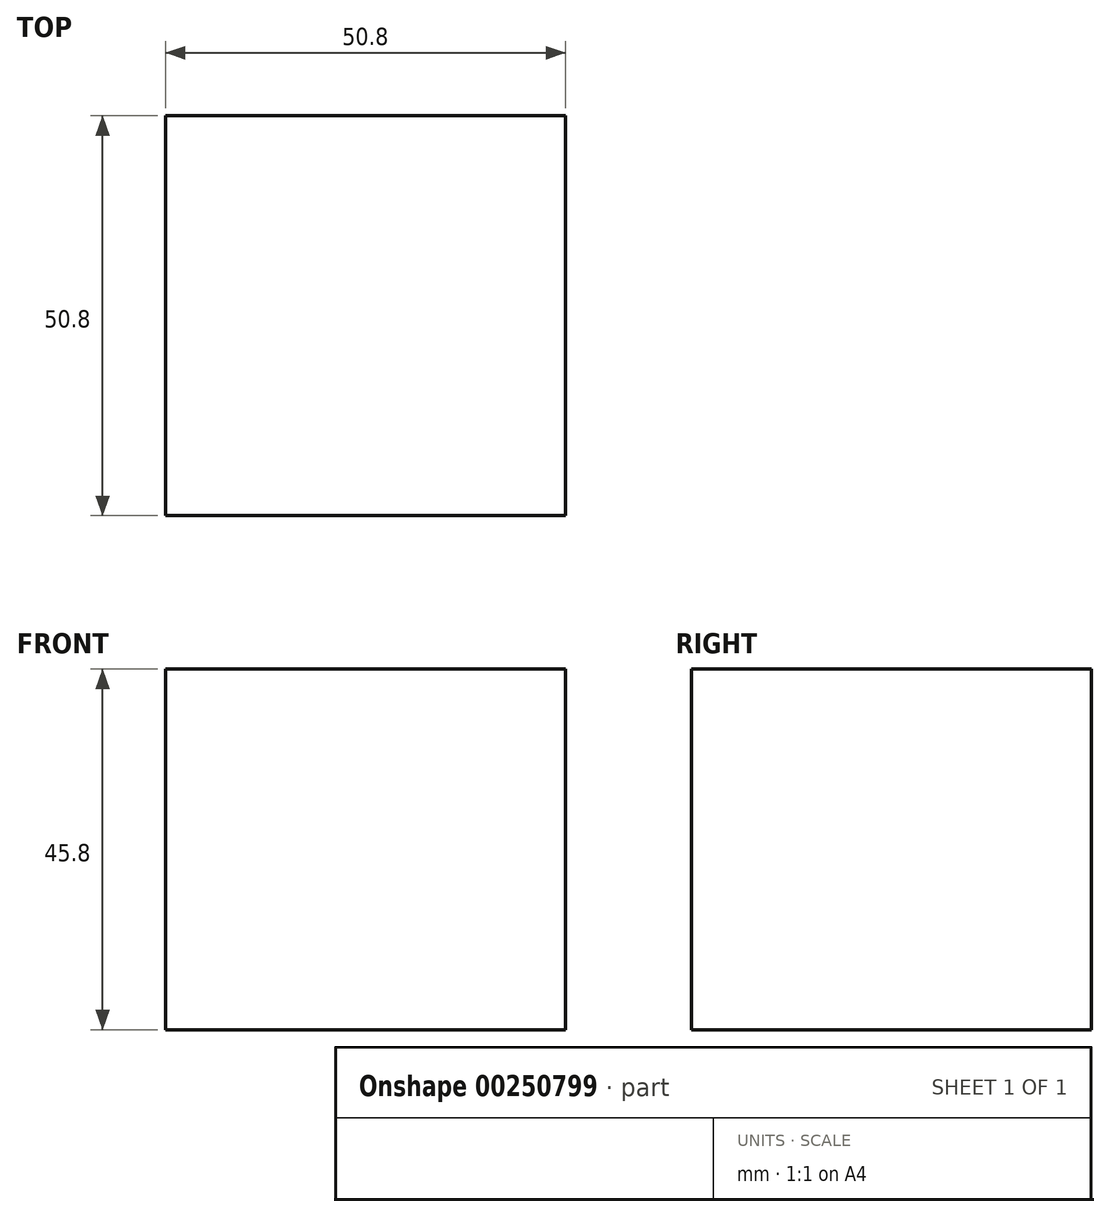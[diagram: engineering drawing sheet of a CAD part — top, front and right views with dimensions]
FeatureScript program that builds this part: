
annotation { "Feature Type Name" : "Feature", "Feature Type Description" : "" }
export const myFeature = defineFeature(function(context is Context, id is Id, definition is map)
    precondition{}
    {
        {
            var Q0;
            Q0=qCreatedBy(makeId("Front.planeOp"),FACE);
            var sketch = newSketch(context, id + "F0", { "sketchPlane" : qUnion([Q0])});
            skLineSegment(sketch, "E0.bottom", {"start": v(25.4, 22.9) * mm, "end": v(-25.4, 22.9) * mm});
            skLineSegment(sketch, "E0.top", {"start": v(25.4, -22.9) * mm, "end": v(-25.4, -22.9) * mm});
            skLineSegment(sketch, "E0.left", {"start": v(25.4, 22.9) * mm, "end": v(25.4, -22.9) * mm});
            skLineSegment(sketch, "E0.right", {"start": v(-25.4, 22.9) * mm, "end": v(-25.4, -22.9) * mm});
            skPoint(sketch, "E0.middle", {"position": v(0, 0) * mm});
            skSolve(sketch);
        }
        {
            var Q0;
            Q0 = qSketchRegion(id + "F0", true);
            extrude(context, id + "F1", {"entities" : qUnion([Q0]), "endBound" : BoundingType.SYMMETRIC, "depth" : 50.8 * mm});
        }
    });
